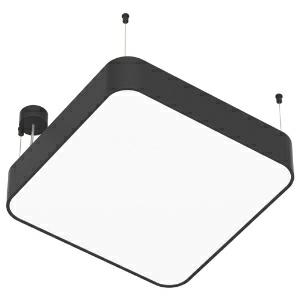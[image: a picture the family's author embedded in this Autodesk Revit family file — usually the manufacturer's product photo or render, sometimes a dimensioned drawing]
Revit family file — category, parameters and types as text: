
# Revit family: smoothy_41150
name_source: partatom
category: Leuchten
revit_build: Autodesk Revit 2016 (Build: 20190508_0715(x64)
units: mm (PartAtom-declared; Revit-internal decimal feet)

## family parameters
Basisbauteil = Fläche
Beim Laden mit Abzugskörper schneiden = Nein
Bemaßung runder Anschluss = Durchmesser verwenden
Gemeinsam genutzt = Nein
Lichtquelle = Nein
Raumberechnungspunkt = Nein
Teiletyp = Normal

## types (1)
- 41150-D01 (4 x LED, 1880 lm, 11.2 W, 3000K)
    Approval mark = CE
    Beschreibung = SMOOTHY
    CIE Flux Codes = 47 78 95 100 74
    Color Rendering = 1B/80…89
    Color Temperature = 3000K
    Height = 120 mm
    Hersteller = Prolicht
    Lamp Light Flux = 1880 lm
    Lamp Power = 11.2 W
    Lamp count = 4
    Lampe = 4 x LED
    Length = 600 mm
    Luminous efficacy = 124 lm/W
    ModVariant = Nein
    Modell = 41150
    Mounting Place = Ceiling
    Mounting Type = Pendant
    Number of Poles = 1
    OnlyDefault = Ja
    Power Factor = 1
    Product Name = SMOOTHY
    Product group = Suspended lights
    ProductGroupID = 941
    Protection Class = Protection class I
    Protection Degree = IP 20
    RLX_Detail_Level = 1
    RlxData = <blob elided: 36445 chars, md5=e89b9124>
    Scheinlast = 45 VA
    Socket = socket
    Standby Power = 0 W
    System Light Flux = 5572 lm
    System Power = 45 W
    Typenbild = 41150.jpg
    Typenkommentare = DIFFUSER Opal (01)
    URL = http://relux.com
    VarID = 41150-d01
    Voltage = 0 V
    Vorgabe-Ansicht = 1800 mm
    Weight = 0.00 kg
    Width = 600 mm

## geometry (parser evidence)
native form markers: Sweep x14
no freeform markers — native parametric forms only
